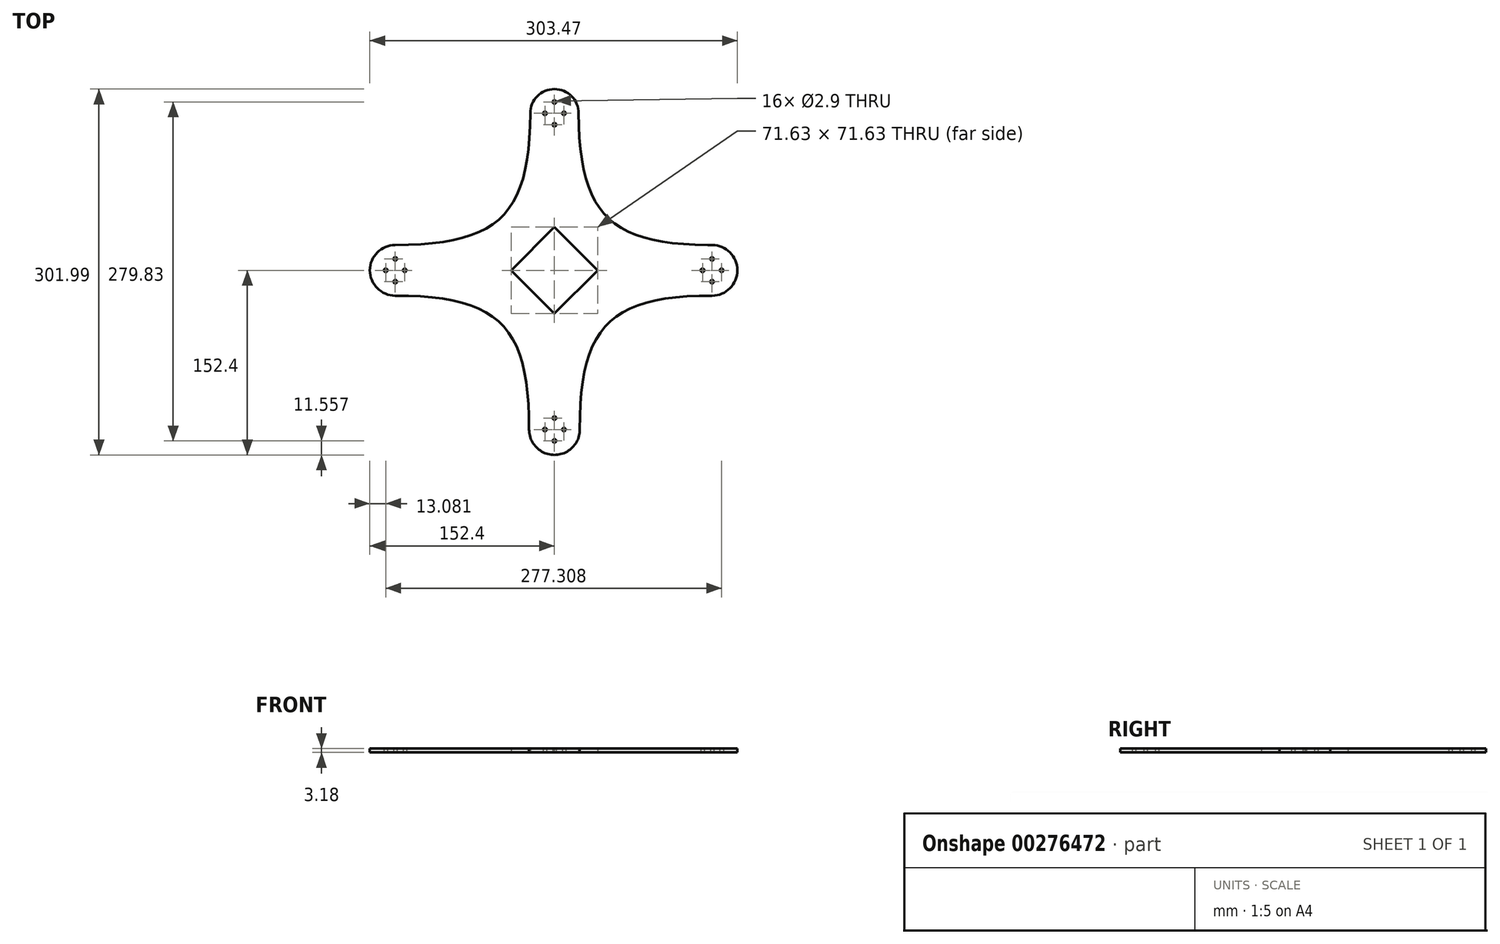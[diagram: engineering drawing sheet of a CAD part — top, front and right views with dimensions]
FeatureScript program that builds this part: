
annotation { "Feature Type Name" : "Feature", "Feature Type Description" : "" }
export const myFeature = defineFeature(function(context is Context, id is Id, definition is map)
    precondition{}
    {
        {
            var Q0;
            Q0=qCreatedBy(makeId("Top.planeOp"),FACE);
            var sketch = newSketch(context, id + "F0", { "sketchPlane" : qUnion([Q0])});
            skLineSegment(sketch, "E0", {"start": v(0, 0) * mm, "end": v(151.07, 0) * mm});
            skLineSegment(sketch, "E1", {"start": v(0, -20.96) * mm, "end": v(0, -152.4) * mm});
            skLineSegment(sketch, "E2", {"start": v(0, 35.81) * mm, "end": v(0, 149.59) * mm});
            skLineSegment(sketch, "E3", {"start": v(0, 149.59) * mm, "end": v(0, 129.59) * mm});
            skCircle(sketch, "E4", {"center": v(0, 129.59) * mm, "radius": 20 * mm});
            skLineSegment(sketch, "E5", {"start": v(0, 129.59) * mm, "end": v(20, 129.59) * mm});
            skLineSegment(sketch, "E6", {"start": v(0, 129.59) * mm, "end": v(-20, 129.59) * mm});
            skLineSegment(sketch, "E7", {"start": v(151.07, 0) * mm, "end": v(130.12, 0) * mm});
            skLineSegment(sketch, "E8", {"start": v(0, -152.4) * mm, "end": v(0, -131.44) * mm});
            skCircle(sketch, "E9", {"center": v(130.12, 0) * mm, "radius": 20.96 * mm});
            skCircle(sketch, "E10", {"center": v(0, -131.44) * mm, "radius": 20.96 * mm});
            skLineSegment(sketch, "E11", {"start": v(130.12, 0) * mm, "end": v(130.12, 20.96) * mm});
            skLineSegment(sketch, "E12", {"start": v(130.12, 20.96) * mm, "end": v(130.12, -20.96) * mm});
            skLineSegment(sketch, "E13", {"start": v(0, -131.44) * mm, "end": v(-20.96, -131.44) * mm});
            skLineSegment(sketch, "E14", {"start": v(-20.96, -131.44) * mm, "end": v(20.96, -131.44) * mm});
            skLineSegment(sketch, "E15", {"start": v(129.4, -20.94) * mm, "end": v(130.12, -20.96) * mm});
            skLineSegment(sketch, "E16.trimOffspring", {"start": v(129.4, 20.94) * mm, "end": v(130.12, 20.95) * mm});
            skLineSegment(sketch, "E17", {"start": v(-35.81, 0) * mm, "end": v(-152.4, 0) * mm});
            skLineSegment(sketch, "E18", {"start": v(-152.4, 0) * mm, "end": v(-131.44, 0) * mm});
            skCircle(sketch, "E19", {"center": v(-131.44, 0) * mm, "radius": 20.96 * mm});
            skLineSegment(sketch, "E20", {"start": v(-131.44, 0) * mm, "end": v(-131.44, 20.96) * mm});
            skLineSegment(sketch, "E21", {"start": v(-131.44, 20.96) * mm, "end": v(-131.44, -20.96) * mm});
            skFitSpline(sketch, "E22", {"points": [v(-131.44, 20.96) * mm, v(-20, 129.59) * mm], "startDerivative": vector(256.95, 0) * mm, "endDerivative": vector(0.92, 249.7) * mm});
            skFitSpline(sketch, "E23", {"points": [v(20, 129.59) * mm, v(129.4, 20.94) * mm], "startDerivative": vector(0.92, -249.7) * mm, "endDerivative": vector(250.84, -0.04) * mm});
            skFitSpline(sketch, "E24", {"points": [v(130.12, -20.96) * mm, v(20.96, -131.44) * mm], "startDerivative": vector(-252.5, 0) * mm, "endDerivative": vector(0.94, -255.27) * mm});
            skFitSpline(sketch, "E25", {"points": [v(-20.96, -131.44) * mm, v(-131.44, -20.96) * mm], "startDerivative": vector(0.94, 255.27) * mm, "endDerivative": vector(-256.49, 0) * mm});
            skLineSegment(sketch, "E26.trimOffspring", {"start": v(126.37, 20.96) * mm, "end": v(130.12, 20.96) * mm});
            skLineSegment(sketch, "E27.trimOffspring", {"start": v(20.55, -20.96) * mm, "end": v(0, -20.96) * mm});
            skLineSegment(sketch, "E28.trimOffspring", {"start": v(-20.95, -131.3) * mm, "end": v(-20.95, -131.45) * mm});
            skLineSegment(sketch, "E29.trimOffspring", {"start": v(20.95, -131.3) * mm, "end": v(20.96, -131.45) * mm});
            skLineSegment(sketch, "E30", {"start": v(-131.44, 0) * mm, "end": v(-131.44, 9.4) * mm});
            skLineSegment(sketch, "E31", {"start": v(-131.44, 0) * mm, "end": v(-131.44, -9.4) * mm});
            skLineSegment(sketch, "E32", {"start": v(-131.44, 0) * mm, "end": v(-123.57, 0) * mm});
            skLineSegment(sketch, "E33", {"start": v(-131.44, 0) * mm, "end": v(-139.32, 0) * mm});
            skCircle(sketch, "E34", {"center": v(-131.44, 9.4) * mm, "radius": 1.45 * mm});
            skCircle(sketch, "E35", {"center": v(-123.57, 0) * mm, "radius": 1.45 * mm});
            skCircle(sketch, "E36", {"center": v(-131.44, -9.4) * mm, "radius": 1.45 * mm});
            skCircle(sketch, "E37", {"center": v(-139.32, 0) * mm, "radius": 1.45 * mm});
            skLineSegment(sketch, "E38", {"start": v(0, 129.59) * mm, "end": v(0, 138.99) * mm});
            skLineSegment(sketch, "E39", {"start": v(0, 129.59) * mm, "end": v(0, 120.2) * mm});
            skLineSegment(sketch, "E40", {"start": v(0, 129.59) * mm, "end": v(7.87, 129.59) * mm});
            skLineSegment(sketch, "E41", {"start": v(0, 129.59) * mm, "end": v(-7.87, 129.59) * mm});
            skCircle(sketch, "E42", {"center": v(0, 138.99) * mm, "radius": 1.45 * mm});
            skCircle(sketch, "E43", {"center": v(7.87, 129.59) * mm, "radius": 1.45 * mm});
            skCircle(sketch, "E44", {"center": v(0, 120.2) * mm, "radius": 1.45 * mm});
            skCircle(sketch, "E45", {"center": v(-7.87, 129.59) * mm, "radius": 1.45 * mm});
            skLineSegment(sketch, "E46", {"start": v(130.12, 0) * mm, "end": v(130.12, 9.4) * mm});
            skLineSegment(sketch, "E47", {"start": v(130.12, 0) * mm, "end": v(130.12, -9.4) * mm});
            skLineSegment(sketch, "E48", {"start": v(130.12, 0) * mm, "end": v(137.99, 0) * mm});
            skLineSegment(sketch, "E49", {"start": v(130.12, 0) * mm, "end": v(122.24, 0) * mm});
            skCircle(sketch, "E50", {"center": v(122.24, 0) * mm, "radius": 1.45 * mm});
            skCircle(sketch, "E51", {"center": v(130.12, 9.4) * mm, "radius": 1.45 * mm});
            skCircle(sketch, "E52", {"center": v(137.99, 0) * mm, "radius": 1.45 * mm});
            skCircle(sketch, "E53", {"center": v(130.12, -9.4) * mm, "radius": 1.45 * mm});
            skLineSegment(sketch, "E54", {"start": v(0, -131.44) * mm, "end": v(0, -122.05) * mm});
            skLineSegment(sketch, "E55", {"start": v(0, -131.44) * mm, "end": v(0, -140.84) * mm});
            skLineSegment(sketch, "E56", {"start": v(0, -131.44) * mm, "end": v(7.87, -131.44) * mm});
            skLineSegment(sketch, "E57", {"start": v(0, -131.44) * mm, "end": v(-7.87, -131.44) * mm});
            skCircle(sketch, "E58", {"center": v(-7.87, -131.44) * mm, "radius": 1.45 * mm});
            skCircle(sketch, "E59", {"center": v(0, -122.05) * mm, "radius": 1.45 * mm});
            skCircle(sketch, "E60", {"center": v(7.87, -131.44) * mm, "radius": 1.45 * mm});
            skCircle(sketch, "E61", {"center": v(0, -140.84) * mm, "radius": 1.45 * mm});
            skLineSegment(sketch, "E62", {"start": v(0, 0) * mm, "end": v(0, 35.81) * mm});
            skLineSegment(sketch, "E63", {"start": v(0, -20.96) * mm, "end": v(0, -35.81) * mm});
            skLineSegment(sketch, "E64", {"start": v(-25.4, 0) * mm, "end": v(-45.95, 0) * mm});
            skLineSegment(sketch, "E65", {"start": v(0, 35.81) * mm, "end": v(35.81, 0) * mm});
            skLineSegment(sketch, "E66", {"start": v(0, -35.81) * mm, "end": v(35.81, 0) * mm});
            skLineSegment(sketch, "E67", {"start": v(-35.81, 0) * mm, "end": v(0, 35.81) * mm});
            skLineSegment(sketch, "E68", {"start": v(0, -35.81) * mm, "end": v(-35.81, 0) * mm});
            skSolve(sketch);
        }
        {
            var Q0;
            Q0=qSketchRegion(id+"F0",true);
            extrude(context, id + "F1", {"entities" : qUnion([Q0]), "depth" : 3.17 * mm});
        }
    });
